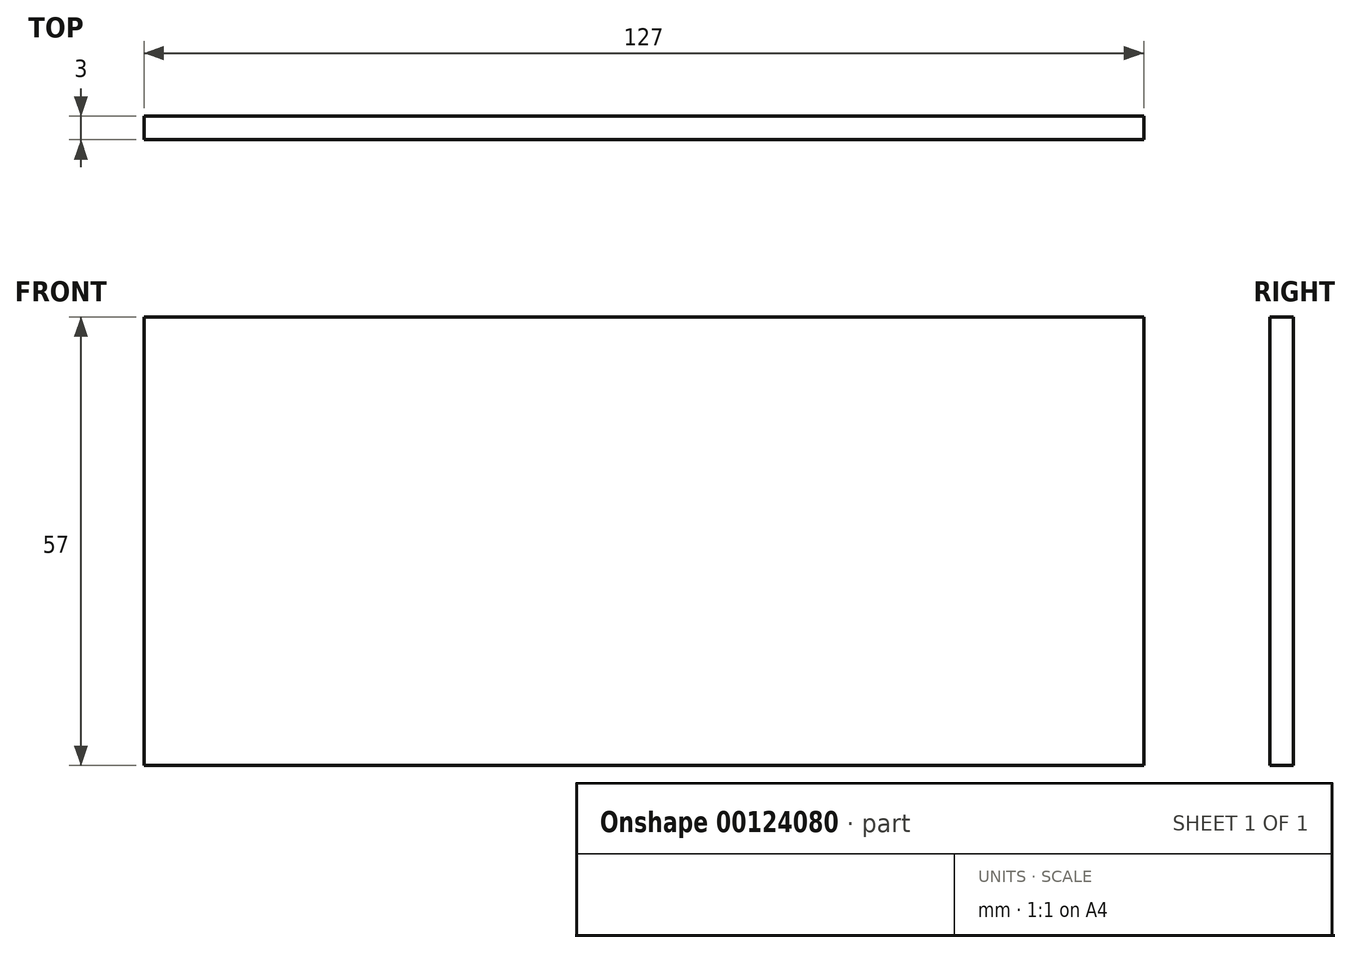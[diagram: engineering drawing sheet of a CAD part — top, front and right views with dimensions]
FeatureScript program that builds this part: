
annotation { "Feature Type Name" : "Feature", "Feature Type Description" : "" }
export const myFeature = defineFeature(function(context is Context, id is Id, definition is map)
    precondition{}
    {
        {
            var Q0;
            Q0=qCreatedBy(makeId("Front.planeOp"),FACE);
            var sketch = newSketch(context, id + "F0", { "sketchPlane" : qUnion([Q0])});
            skLineSegment(sketch, "E0.bottom", {"start": v(-33.57, 47.92) * mm, "end": v(55.33, 47.92) * mm});
            skLineSegment(sketch, "E0.top", {"start": v(-33.57, -15.58) * mm, "end": v(55.33, -15.58) * mm});
            skLineSegment(sketch, "E0.left", {"start": v(-33.57, 47.92) * mm, "end": v(-33.57, -15.58) * mm});
            skLineSegment(sketch, "E0.right", {"start": v(55.33, 47.92) * mm, "end": v(55.33, -15.58) * mm});
            skLineSegment(sketch, "E1.bottom", {"start": v(-22.05, 37.07) * mm, "end": v(43.99, 37.07) * mm});
            skLineSegment(sketch, "E1.top", {"start": v(-22.05, 24.88) * mm, "end": v(43.99, 24.88) * mm});
            skLineSegment(sketch, "E1.left", {"start": v(-22.05, 37.07) * mm, "end": v(-22.05, 24.88) * mm});
            skLineSegment(sketch, "E1.right", {"start": v(43.99, 37.07) * mm, "end": v(43.99, 24.88) * mm});
            skLineSegment(sketch, "E2.bottom", {"start": v(-21.16, 5.79) * mm, "end": v(44.88, 5.79) * mm});
            skLineSegment(sketch, "E2.top", {"start": v(-21.16, -6.4) * mm, "end": v(44.88, -6.4) * mm});
            skLineSegment(sketch, "E2.left", {"start": v(-21.16, 5.79) * mm, "end": v(-21.16, -6.4) * mm});
            skLineSegment(sketch, "E2.right", {"start": v(44.88, 5.79) * mm, "end": v(44.88, -6.4) * mm});
            skSolve(sketch);
        }
        {
            var Q0;
            Q0=makeQuery(id+"F0.imprint","IMPRINT",FACE,{"disambiguationData":[TD([[makeQuery(id+"F0.imprint","IMPRINT",EDGE,{"derivedFrom":sQuery(id+"F0.wireOp",EDGE,"E0.bottom")}),-1.0]])]});
            extrude(context, id + "F1", {"entities" : qUnion([Q0]), "depth" : 6.35 * mm});
        }
        {
            var Q0;
            Q0=makeQuery(id+"F1.opExtrude","SWEPT_BODY",BODY,{"disambiguationData":[OSD([sQuery(id+"F0.wireOp",EDGE,"E0.bottom"),sQuery(id+"F0.wireOp",EDGE,"E0.top"),sQuery(id+"F0.wireOp",EDGE,"E0.left"),sQuery(id+"F0.wireOp",EDGE,"E0.right"),sQuery(id+"F0.wireOp",EDGE,"E1.bottom"),sQuery(id+"F0.wireOp",EDGE,"E1.top"),sQuery(id+"F0.wireOp",EDGE,"E1.left"),sQuery(id+"F0.wireOp",EDGE,"E1.right"),sQuery(id+"F0.wireOp",EDGE,"E2.bottom"),sQuery(id+"F0.wireOp",EDGE,"E2.top"),sQuery(id+"F0.wireOp",EDGE,"E2.left"),sQuery(id+"F0.wireOp",EDGE,"E2.right")])]});
            deleteBodies(context, id + "F2", {"entities" : qUnion([Q0])});
        }
        {
            var Q0;
            Q0=qCreatedBy(makeId("Front.planeOp"),FACE);
            var sketch = newSketch(context, id + "F3", { "sketchPlane" : qUnion([Q0])});
            skCircle(sketch, "E3", {"center": v(-8.64, 16.24) * mm, "radius": 60.33 * mm});
            skCircle(sketch, "E4", {"center": v(-8.64, 16.24) * mm, "radius": 7.94 * mm});
            skCircle(sketch, "E5", {"center": v(-8.64, 16.24) * mm, "radius": 19.05 * mm, "construction": true});
            skSolve(sketch);
        }
        {
            var Q0;
            Q0=makeQuery(id+"F3.imprint","IMPRINT",FACE,{"disambiguationData":[TD([[makeQuery(id+"F3.imprint","IMPRINT",EDGE,{"derivedFrom":sQuery(id+"F3.wireOp",EDGE,"E3")}),1.0]])]});
            extrude(context, id + "F4", {"entities" : qUnion([Q0]), "depth" : 2.54 * mm});
        }
        {
            var Q0;
            Q0=makeQuery(id+"F4.opExtrude","SWEPT_BODY",BODY,{"disambiguationData":[OSD([sQuery(id+"F3.wireOp",EDGE,"E3"),sQuery(id+"F3.wireOp",EDGE,"E4")])]});
            deleteBodies(context, id + "F5", {"entities" : qUnion([Q0])});
        }
        {
            var Q0;
            Q0=qCreatedBy(makeId("Front.planeOp"),FACE);
            var sketch = newSketch(context, id + "F6", { "sketchPlane" : qUnion([Q0])});
            skLineSegment(sketch, "E6.bottom", {"start": v(-74.57, 37.24) * mm, "end": v(52.43, 37.24) * mm});
            skLineSegment(sketch, "E6.top", {"start": v(-74.57, -19.76) * mm, "end": v(52.43, -19.76) * mm});
            skLineSegment(sketch, "E6.left", {"start": v(-74.57, 37.24) * mm, "end": v(-74.57, -19.76) * mm});
            skLineSegment(sketch, "E6.right", {"start": v(52.43, 37.24) * mm, "end": v(52.43, -19.76) * mm});
            skSolve(sketch);
        }
        {
            var Q0;
            Q0 = qSketchRegion(id + "F6", true);
            extrude(context, id + "F7", {"entities" : qUnion([Q0]), "depth" : 3 * mm});
        }
    });
